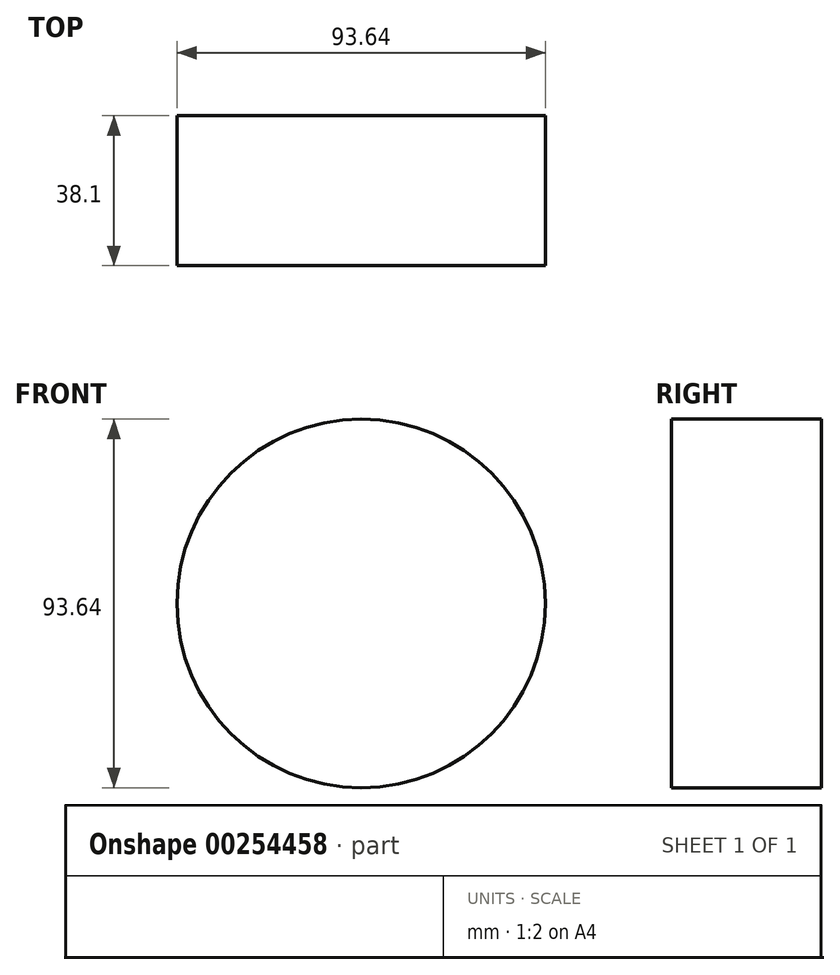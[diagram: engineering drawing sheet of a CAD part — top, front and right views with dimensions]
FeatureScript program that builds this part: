
annotation { "Feature Type Name" : "Feature", "Feature Type Description" : "" }
export const myFeature = defineFeature(function(context is Context, id is Id, definition is map)
    precondition{}
    {
        {
            var Q0;
            Q0=qCreatedBy(makeId("Front.planeOp"),FACE);
            var sketch = newSketch(context, id + "F0", { "sketchPlane" : qUnion([Q0])});
            skCircle(sketch, "E0", {"center": v(0, 0) * mm, "radius": 46.82 * mm});
            skSolve(sketch);
        }
        {
            var Q0;
            Q0=makeQuery(id+"F0.imprint","IMPRINT",FACE,{"disambiguationData":[TD([[makeQuery(id+"F0.imprint","IMPRINT",EDGE,{"derivedFrom":sQuery(id+"F0.wireOp",EDGE,"E0")}),1.0]])]});
            extrude(context, id + "F1", {"entities" : qUnion([Q0]), "oppositeDirection" : true, "depth" : 38.1 * mm});
        }
    });
